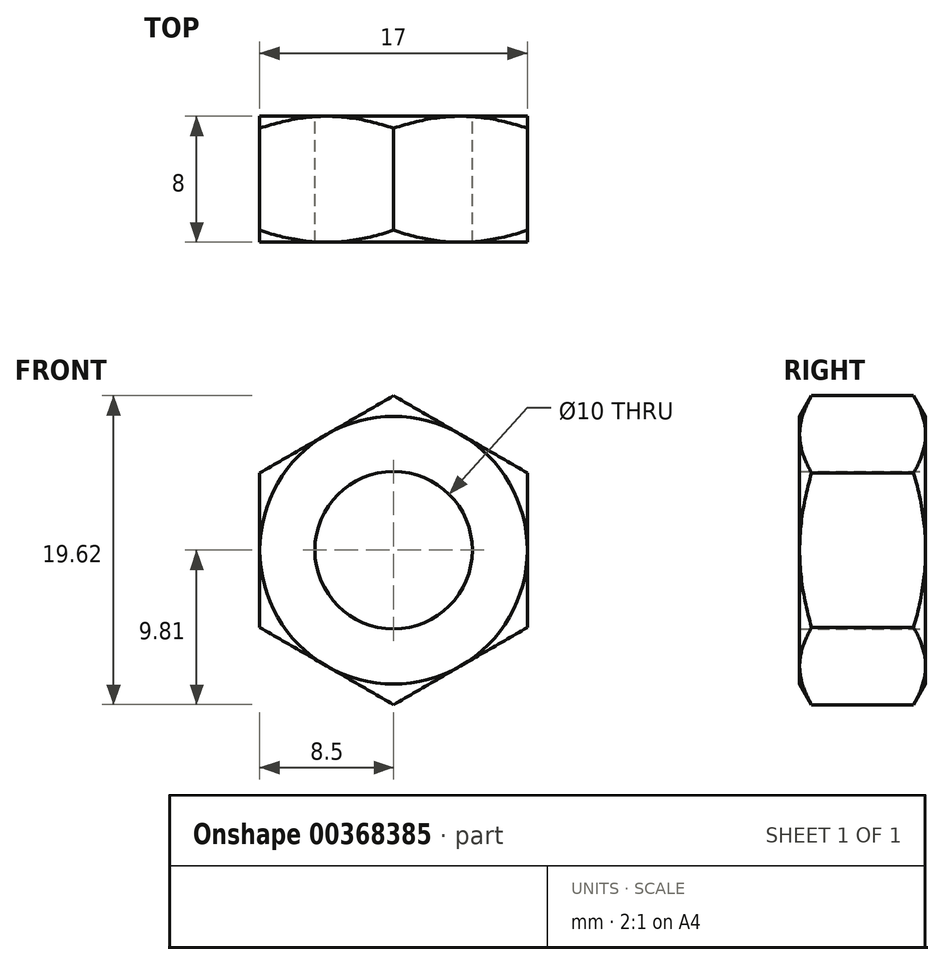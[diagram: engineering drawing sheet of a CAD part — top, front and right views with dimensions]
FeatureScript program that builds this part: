
annotation { "Feature Type Name" : "Feature", "Feature Type Description" : "" }
export const myFeature = defineFeature(function(context is Context, id is Id, definition is map)
    precondition{}
    {
        {
            var Q0;
            Q0=qCreatedBy(makeId("Front.planeOp"),FACE);
            var sketch = newSketch(context, id + "F0", { "sketchPlane" : qUnion([Q0])});
            skCircle(sketch, "E0.cCircle", {"center": v(0, 0) * mm, "radius": 8.5 * mm, "construction": true});
            skLineSegment(sketch, "E0.0", {"start": v(8.5, 4.9) * mm, "end": v(8.5, -4.9) * mm});
            skLineSegment(sketch, "E0.1", {"start": v(8.5, -4.9) * mm, "end": v(0, -9.81) * mm});
            skLineSegment(sketch, "E0.2", {"start": v(0, -9.81) * mm, "end": v(-8.5, -4.9) * mm});
            skLineSegment(sketch, "E0.3", {"start": v(-8.5, -4.9) * mm, "end": v(-8.5, 4.9) * mm});
            skLineSegment(sketch, "E0.4", {"start": v(-8.5, 4.9) * mm, "end": v(0, 9.81) * mm});
            skLineSegment(sketch, "E0.5", {"start": v(0, 9.81) * mm, "end": v(8.5, 4.9) * mm});
            skPoint(sketch, "E0.0.midPoint", {"position": v(8.5, 0) * mm});
            skCircle(sketch, "E1", {"center": v(0, 0) * mm, "radius": 5 * mm});
            skSolve(sketch);
        }
        {
            var Q0;
            Q0=qSketchRegion(id+"F0",true);
            extrude(context, id + "F1", {"entities" : qUnion([Q0]), "depth" : 8 * mm});
        }
        {
            var Q0;
            Q0=qCreatedBy(makeId("Top.planeOp"),FACE);
            var sketch = newSketch(context, id + "F2", { "sketchPlane" : qUnion([Q0])});
            skLineSegment(sketch, "E2", {"start": v(0, 0) * mm, "end": v(0, -8) * mm, "construction": true});
            skLineSegment(sketch, "E3", {"start": v(0, -4) * mm, "end": v(8.5, -4) * mm, "construction": true});
            skPoint(sketch, "E3.endSnap0", {"position": v(0, -4) * mm});
            skLineSegment(sketch, "E4", {"start": v(11.58, 0) * mm, "end": v(11.58, -1.78) * mm});
            skLineSegment(sketch, "E5", {"start": v(11.58, -1.78) * mm, "end": v(8.5, 0) * mm});
            skLineSegment(sketch, "E6", {"start": v(8.5, 0) * mm, "end": v(11.58, 0) * mm});
            skLineSegment(sketch, "E7.MirrorCS", {"start": v(8.5, -8) * mm, "end": v(11.58, -8) * mm});
            skLineSegment(sketch, "E8.MirrorCS", {"start": v(11.58, -6.22) * mm, "end": v(8.5, -8) * mm});
            skLineSegment(sketch, "E9.MirrorCS", {"start": v(11.58, -8) * mm, "end": v(11.58, -6.22) * mm});
            skSolve(sketch);
        }
        {
            var Q0;
            Q0=qSketchRegion(id+"F2",true);
            var Q1;
            Q1=sQuery(id+"F2.wireOp",EDGE,"E2");
            revolve(context, id + "F3", {"operationType" : NewBodyOperationType.REMOVE, "entities" : qUnion([Q0]), "axis" : qUnion([Q1]), "revolveType" : RevolveType.FULL, "oppositeDirection" : true});
        }
    });
